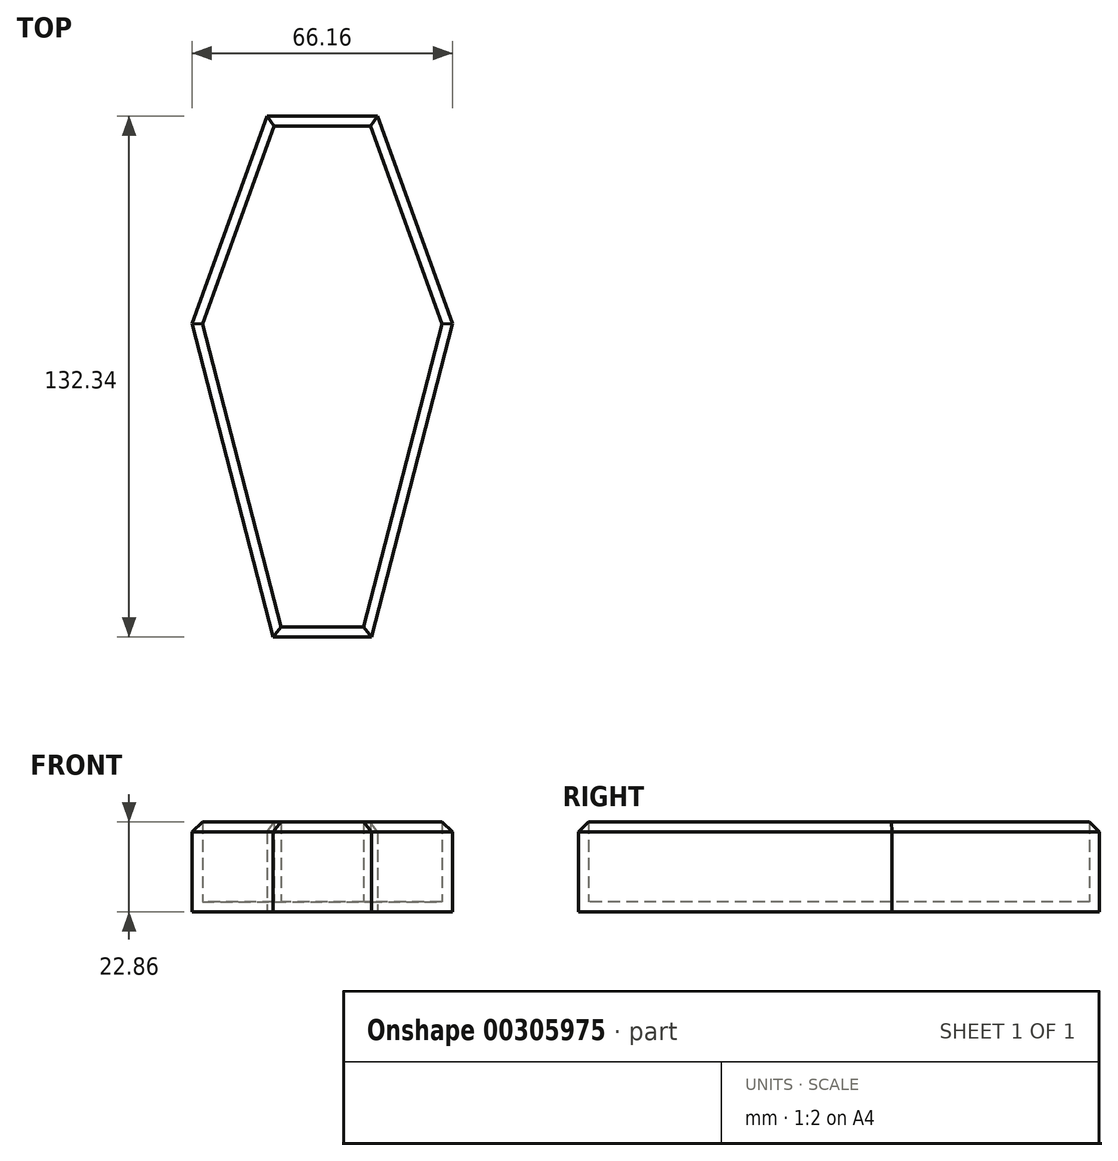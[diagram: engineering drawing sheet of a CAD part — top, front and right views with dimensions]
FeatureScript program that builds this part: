
annotation { "Feature Type Name" : "Feature", "Feature Type Description" : "" }
export const myFeature = defineFeature(function(context is Context, id is Id, definition is map)
    precondition{}
    {
        {
            var Q0;
            Q0=qCreatedBy(makeId("Top.planeOp"),FACE);
            var sketch = newSketch(context, id + "F0", { "sketchPlane" : qUnion([Q0])});
            skLineSegment(sketch, "E0", {"start": v(0, -57.73) * mm, "end": v(0, 74.6) * mm});
            skLineSegment(sketch, "E1", {"start": v(0, 74.6) * mm, "end": v(-13.99, 74.6) * mm});
            skLineSegment(sketch, "E2", {"start": v(-13.99, 74.6) * mm, "end": v(-33.08, 21.94) * mm});
            skLineSegment(sketch, "E3", {"start": v(-33.08, 21.94) * mm, "end": v(-12.5, -57.73) * mm});
            skLineSegment(sketch, "E4", {"start": v(-12.5, -57.73) * mm, "end": v(0, -57.73) * mm});
            skLineSegment(sketch, "E5.MirrorCS", {"start": v(13.99, 74.6) * mm, "end": v(33.08, 21.94) * mm});
            skLineSegment(sketch, "E6.MirrorCS", {"start": v(0, 74.6) * mm, "end": v(13.99, 74.6) * mm});
            skLineSegment(sketch, "E7.MirrorCS", {"start": v(33.08, 21.94) * mm, "end": v(12.5, -57.73) * mm});
            skLineSegment(sketch, "E8.MirrorCS", {"start": v(12.5, -57.73) * mm, "end": v(0, -57.73) * mm});
            skSolve(sketch);
        }
        {
            var Q0;
            Q0=makeQuery(id+"F0.imprint","IMPRINT",FACE,{"disambiguationData":[TD([[makeQuery(id+"F0.imprint","IMPRINT",EDGE,{"derivedFrom":sQuery(id+"F0.wireOp",EDGE,"E0")}),-1.0]])]});
            var Q1;
            Q1=makeQuery(id+"F0.imprint","IMPRINT",FACE,{"disambiguationData":[TD([[makeQuery(id+"F0.imprint","IMPRINT",EDGE,{"derivedFrom":sQuery(id+"F0.wireOp",EDGE,"E0")}),1.0]])]});
            extrude(context, id + "F1", {"entities" : qUnion([Q0, Q1]), "depth" : 25.4 * mm});
        }
        {
            var Q0;
            Q0=makeQuery(id+"F1.opExtrude","CAP_FACE",FACE,{"disambiguationData":[OSD([sQuery(id+"F0.wireOp",EDGE,"E1"),sQuery(id+"F0.wireOp",EDGE,"E2"),sQuery(id+"F0.wireOp",EDGE,"E3"),sQuery(id+"F0.wireOp",EDGE,"E4"),sQuery(id+"F0.wireOp",EDGE,"E5.MirrorCS"),sQuery(id+"F0.wireOp",EDGE,"E6.MirrorCS"),sQuery(id+"F0.wireOp",EDGE,"E7.MirrorCS"),sQuery(id+"F0.wireOp",EDGE,"E8.MirrorCS")])],"isStart":false});
            shell(context, id + "F2", {"entities" : qUnion([Q0]), "thickness" : 2.54 * mm});
        }
        {
            var Q0;
            Q0=makeQuery(id+"F1.opExtrude","CAP_EDGE",EDGE,{"disambiguationData":[OSD([sQuery(id+"F0.wireOp",EDGE,"E7.MirrorCS")])],"isStart":false});
            var Q1;
            Q1=makeQuery(id+"F1.opExtrude","CAP_EDGE",EDGE,{"disambiguationData":[OSD([sQuery(id+"F0.wireOp",EDGE,"E5.MirrorCS")])],"isStart":false});
            var Q2;
            Q2=makeQuery(id+"F1.opExtrude","CAP_EDGE",EDGE,{"disambiguationData":[OSD([sQuery(id+"F0.wireOp",EDGE,"E1"),sQuery(id+"F0.wireOp",EDGE,"E6.MirrorCS")])],"isStart":false});
            var Q3;
            Q3=makeQuery(id+"F1.opExtrude","CAP_EDGE",EDGE,{"disambiguationData":[OSD([sQuery(id+"F0.wireOp",EDGE,"E2")])],"isStart":false});
            var Q4;
            Q4=makeQuery(id+"F1.opExtrude","CAP_EDGE",EDGE,{"disambiguationData":[OSD([sQuery(id+"F0.wireOp",EDGE,"E3")])],"isStart":false});
            var Q5;
            Q5=makeQuery(id+"F1.opExtrude","CAP_EDGE",EDGE,{"disambiguationData":[OSD([sQuery(id+"F0.wireOp",EDGE,"E4"),sQuery(id+"F0.wireOp",EDGE,"E8.MirrorCS")])],"isStart":false});
            chamfer(context, id + "F3", {"entities" : qUnion([Q0, Q1, Q2, Q3, Q4, Q5]), "width" : 5.08 * mm, "tangentPropagation" : true});
        }
    });
